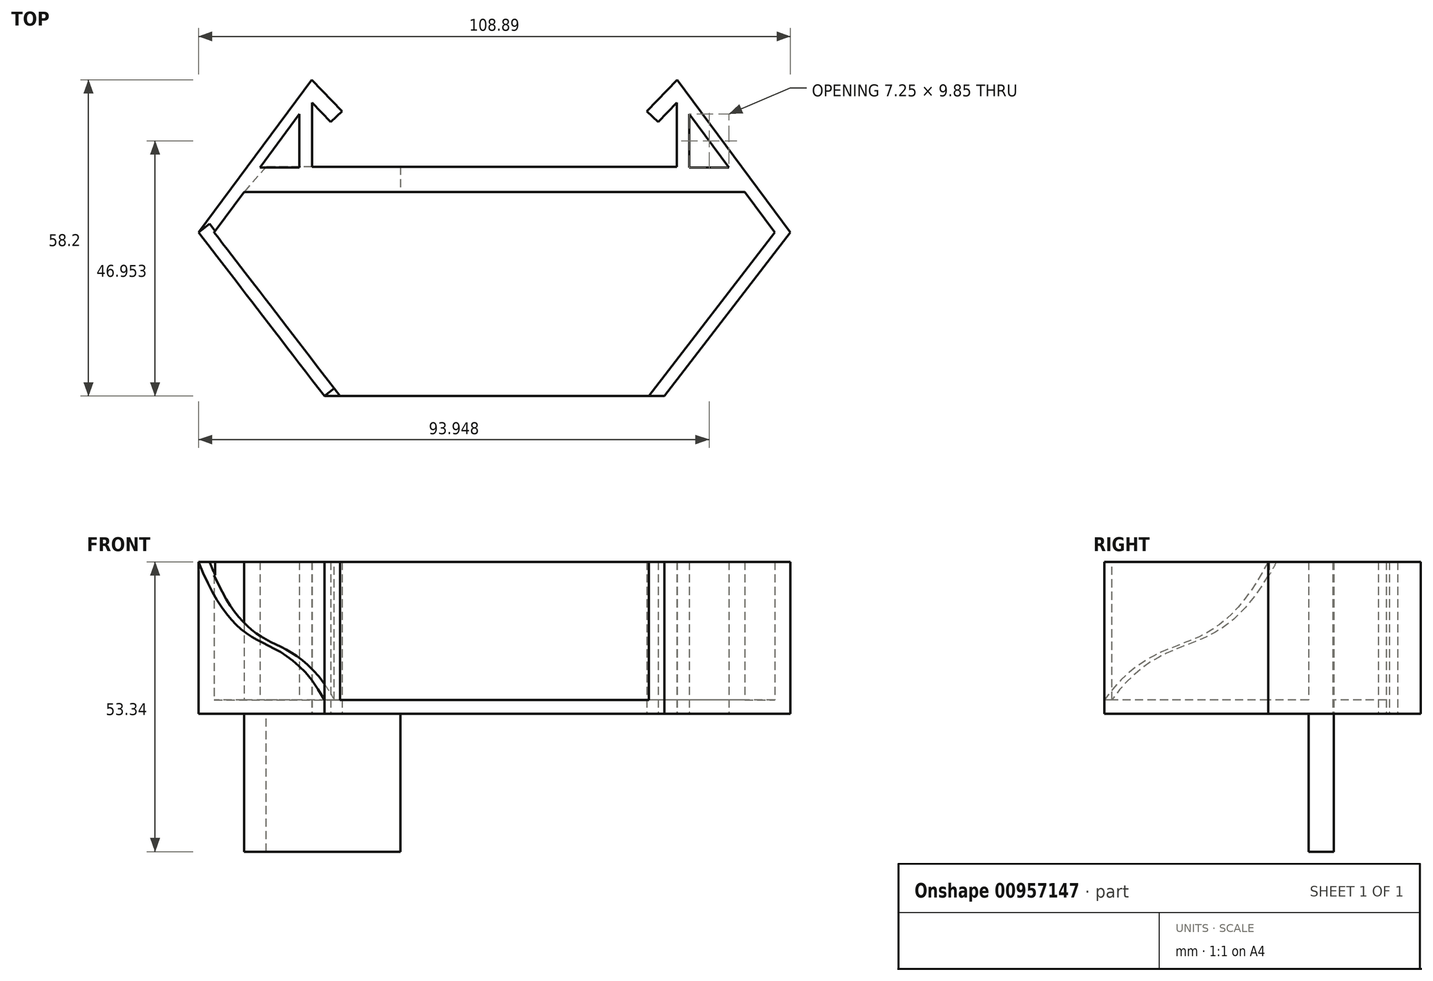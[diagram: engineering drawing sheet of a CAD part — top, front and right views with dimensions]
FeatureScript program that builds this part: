
annotation { "Feature Type Name" : "Feature", "Feature Type Description" : "" }
export const myFeature = defineFeature(function(context is Context, id is Id, definition is map)
    precondition{}
    {
        {
            var Q0;
            Q0=qCreatedBy(makeId("Top.planeOp"),FACE);
            var sketch = newSketch(context, id + "F0", { "sketchPlane" : qUnion([Q0])});
            skLineSegment(sketch, "E0", {"start": v(-16.08, -26.23) * mm, "end": v(15.21, -26.23) * mm});
            skLineSegment(sketch, "E1", {"start": v(15.21, -26.23) * mm, "end": v(38.36, 3.9) * mm});
            skLineSegment(sketch, "E2", {"start": v(38.36, 3.9) * mm, "end": v(17.55, 31.97) * mm});
            skLineSegment(sketch, "E3", {"start": v(17.55, 31.97) * mm, "end": v(11.97, 26.2) * mm});
            skLineSegment(sketch, "E4", {"start": v(11.97, 26.2) * mm, "end": v(14.04, 24.2) * mm});
            skLineSegment(sketch, "E5", {"start": v(14.04, 24.2) * mm, "end": v(17.47, 27.76) * mm});
            skLineSegment(sketch, "E6", {"start": v(17.47, 27.76) * mm, "end": v(17.47, 15.98) * mm});
            skLineSegment(sketch, "E7", {"start": v(17.47, 15.98) * mm, "end": v(-16.08, 15.98) * mm});
            skLineSegment(sketch, "E8", {"start": v(19.8, 25.65) * mm, "end": v(19.8, 15.8) * mm});
            skLineSegment(sketch, "E9", {"start": v(19.8, 15.8) * mm, "end": v(27.04, 15.8) * mm});
            skLineSegment(sketch, "E10", {"start": v(27.04, 15.8) * mm, "end": v(19.8, 25.65) * mm});
            skLineSegment(sketch, "E11", {"start": v(-16.08, 11.34) * mm, "end": v(29.98, 11.34) * mm});
            skLineSegment(sketch, "E12", {"start": v(29.98, 11.34) * mm, "end": v(35.5, 3.9) * mm});
            skLineSegment(sketch, "E13", {"start": v(35.5, 3.9) * mm, "end": v(12.34, -26.23) * mm});
            skLineSegment(sketch, "E14", {"start": v(-16.08, 24.53) * mm, "end": v(-16.08, -46.46) * mm, "construction": true});
            skLineSegment(sketch, "E15.MirrorCS", {"start": v(-46.2, 24.2) * mm, "end": v(-49.64, 27.76) * mm});
            skLineSegment(sketch, "E16.MirrorCS", {"start": v(-44.14, 26.2) * mm, "end": v(-46.2, 24.2) * mm});
            skLineSegment(sketch, "E17.MirrorCS", {"start": v(-49.72, 31.97) * mm, "end": v(-44.14, 26.2) * mm});
            skLineSegment(sketch, "E18.MirrorCS", {"start": v(-62.15, 11.34) * mm, "end": v(-67.66, 3.9) * mm});
            skLineSegment(sketch, "E19.MirrorCS", {"start": v(-49.64, 15.98) * mm, "end": v(-16.08, 15.98) * mm});
            skLineSegment(sketch, "E20.MirrorCS", {"start": v(-70.53, 3.9) * mm, "end": v(-49.72, 31.97) * mm});
            skLineSegment(sketch, "E21.MirrorCS", {"start": v(-51.96, 15.8) * mm, "end": v(-59.21, 15.8) * mm});
            skLineSegment(sketch, "E22.MirrorCS", {"start": v(-59.21, 15.8) * mm, "end": v(-51.96, 25.65) * mm});
            skLineSegment(sketch, "E23.MirrorCS", {"start": v(-16.08, 11.34) * mm, "end": v(-62.15, 11.34) * mm});
            skLineSegment(sketch, "E24.MirrorCS", {"start": v(-47.38, -26.23) * mm, "end": v(-70.53, 3.9) * mm});
            skLineSegment(sketch, "E25.MirrorCS", {"start": v(-49.64, 27.76) * mm, "end": v(-49.64, 15.98) * mm});
            skLineSegment(sketch, "E26.MirrorCS", {"start": v(-51.96, 25.65) * mm, "end": v(-51.96, 15.8) * mm});
            skLineSegment(sketch, "E27.MirrorCS", {"start": v(-67.66, 3.9) * mm, "end": v(-44.51, -26.23) * mm});
            skLineSegment(sketch, "E28.MirrorCS", {"start": v(-16.08, -26.23) * mm, "end": v(-47.38, -26.23) * mm});
            skSolve(sketch);
        }
        {
            var Q0;
            {var subQ1=sQuery(id+"F0.wireOp",EDGE,"E1");Q0=makeQuery(id+"F0.imprint","IMPRINT",FACE,{"disambiguationData":[TD([[makeQuery(id+"F0.imprint","IMPRINT",EDGE,{"derivedFrom":subQ1}),1.0]])]});}
            extrude(context, id + "F1", {"entities" : qUnion([Q0]), "depth" : 25.4 * mm, "offsetDistance" : 25.4 * mm});
        }
        {
            var Q0;
            Q0=makeQuery(id+"F1.opExtrude","SWEPT_FACE",FACE,{"disambiguationData":[OSD([sQuery(id+"F0.wireOp",EDGE,"E24.MirrorCS")])]});
            var sketch = newSketch(context, id + "F2", { "sketchPlane" : qUnion([Q0])});
            skFitSpline(sketch, "E29", {"points": [v(-46.07, 25.4) * mm, v(-29.95, 11.58) * mm, v(-8.07, 0) * mm], "startDerivative": vector(32.15, -49.1) * mm, "endDerivative": vector(43.73, -48.68) * mm});
            skLineSegment(sketch, "E30", {"start": v(-46.07, 25.4) * mm, "end": v(49.78, 25.4) * mm});
            skLineSegment(sketch, "E31", {"start": v(49.78, 25.4) * mm, "end": v(-8.07, 0) * mm});
            skSolve(sketch);
        }
        {
            var Q0;
            {var subQ0=sQuery(id+"F2.wireOp",EDGE,"E29");Q0=makeQuery(id+"F2.imprint","IMPRINT",FACE,{"disambiguationData":[TD([[makeQuery(id+"F2.imprint","IMPRINT",EDGE,{"derivedFrom":subQ0}),1.0]])]});}
            extrude(context, id + "F3", {"entities" : qUnion([Q0]), "operationType" : NewBodyOperationType.REMOVE, "oppositeDirection" : true, "depth" : 2.54 * mm, "offsetDistance" : 25.4 * mm});
        }
        {
            var Q0;
            Q0=makeQuery(id+"F0.imprint","IMPRINT",FACE,{"disambiguationData":[TD([[makeQuery(id+"F0.imprint","IMPRINT",EDGE,{"derivedFrom":sQuery(id+"F0.wireOp",EDGE,"E11")}),-1.0]])]});
            var Q1;
            {var subQ1=sQuery(id+"F0.wireOp",EDGE,"E1");Q1=makeQuery(id+"F0.imprint","IMPRINT",FACE,{"disambiguationData":[TD([[makeQuery(id+"F0.imprint","IMPRINT",EDGE,{"derivedFrom":subQ1}),1.0]])]});}
            var Q2;
            Q2=makeQuery(id+"F0.imprint","IMPRINT",FACE,{"disambiguationData":[TD([[makeQuery(id+"F0.imprint","IMPRINT",EDGE,{"derivedFrom":sQuery(id+"F0.wireOp",EDGE,"E21.MirrorCS")}),-1.0]])]});
            extrude(context, id + "F4", {"entities" : qUnion([Q0, Q1, Q2]), "operationType" : NewBodyOperationType.ADD, "oppositeDirection" : true, "depth" : 2.54 * mm, "offsetDistance" : 25.4 * mm});
        }
        {
            var Q0;
            Q0=makeQuery(id+"F4.opExtrude","CAP_FACE",FACE,{"disambiguationData":[OSD([sQuery(id+"F0.wireOp",EDGE,"E0"),sQuery(id+"F0.wireOp",EDGE,"E1"),sQuery(id+"F0.wireOp",EDGE,"E2"),sQuery(id+"F0.wireOp",EDGE,"E3"),sQuery(id+"F0.wireOp",EDGE,"E4"),sQuery(id+"F0.wireOp",EDGE,"E5"),sQuery(id+"F0.wireOp",EDGE,"E6"),sQuery(id+"F0.wireOp",EDGE,"E7"),sQuery(id+"F0.wireOp",EDGE,"E8"),sQuery(id+"F0.wireOp",EDGE,"E9"),sQuery(id+"F0.wireOp",EDGE,"E10"),sQuery(id+"F0.wireOp",EDGE,"E15.MirrorCS"),sQuery(id+"F0.wireOp",EDGE,"E16.MirrorCS"),sQuery(id+"F0.wireOp",EDGE,"E17.MirrorCS"),sQuery(id+"F0.wireOp",EDGE,"E19.MirrorCS"),sQuery(id+"F0.wireOp",EDGE,"E20.MirrorCS"),sQuery(id+"F0.wireOp",EDGE,"E24.MirrorCS"),sQuery(id+"F0.wireOp",EDGE,"E25.MirrorCS"),sQuery(id+"F0.wireOp",EDGE,"E28.MirrorCS")])],"isStart":false});
            var sketch = newSketch(context, id + "F5", { "sketchPlane" : qUnion([Q0])});
            skLineSegment(sketch, "E32.bottom", {"start": v(-33.36, -15.98) * mm, "end": v(-58.45, -15.98) * mm});
            skLineSegment(sketch, "E32.top", {"start": v(-33.36, -11.34) * mm, "end": v(-62.17, -11.34) * mm});
            skLineSegment(sketch, "E32.left", {"start": v(-33.36, -15.98) * mm, "end": v(-33.36, -11.34) * mm});
            skLineSegment(sketch, "E32.right", {"start": v(-58.08, -15.98) * mm, "end": v(-62.17, -11.34) * mm});
            skSolve(sketch);
        }
        {
            var Q0;
            Q0=makeQuery(id+"F5.imprint","IMPRINT",FACE,{"disambiguationData":[TD([[makeQuery(id+"F5.imprint","IMPRINT",EDGE,{"derivedFrom":sQuery(id+"F5.wireOp",EDGE,"E32.top")}),1.0]])]});
            extrude(context, id + "F6", {"entities" : qUnion([Q0]), "operationType" : NewBodyOperationType.ADD, "depth" : 25.4 * mm, "offsetDistance" : 25.4 * mm});
        }
    });
